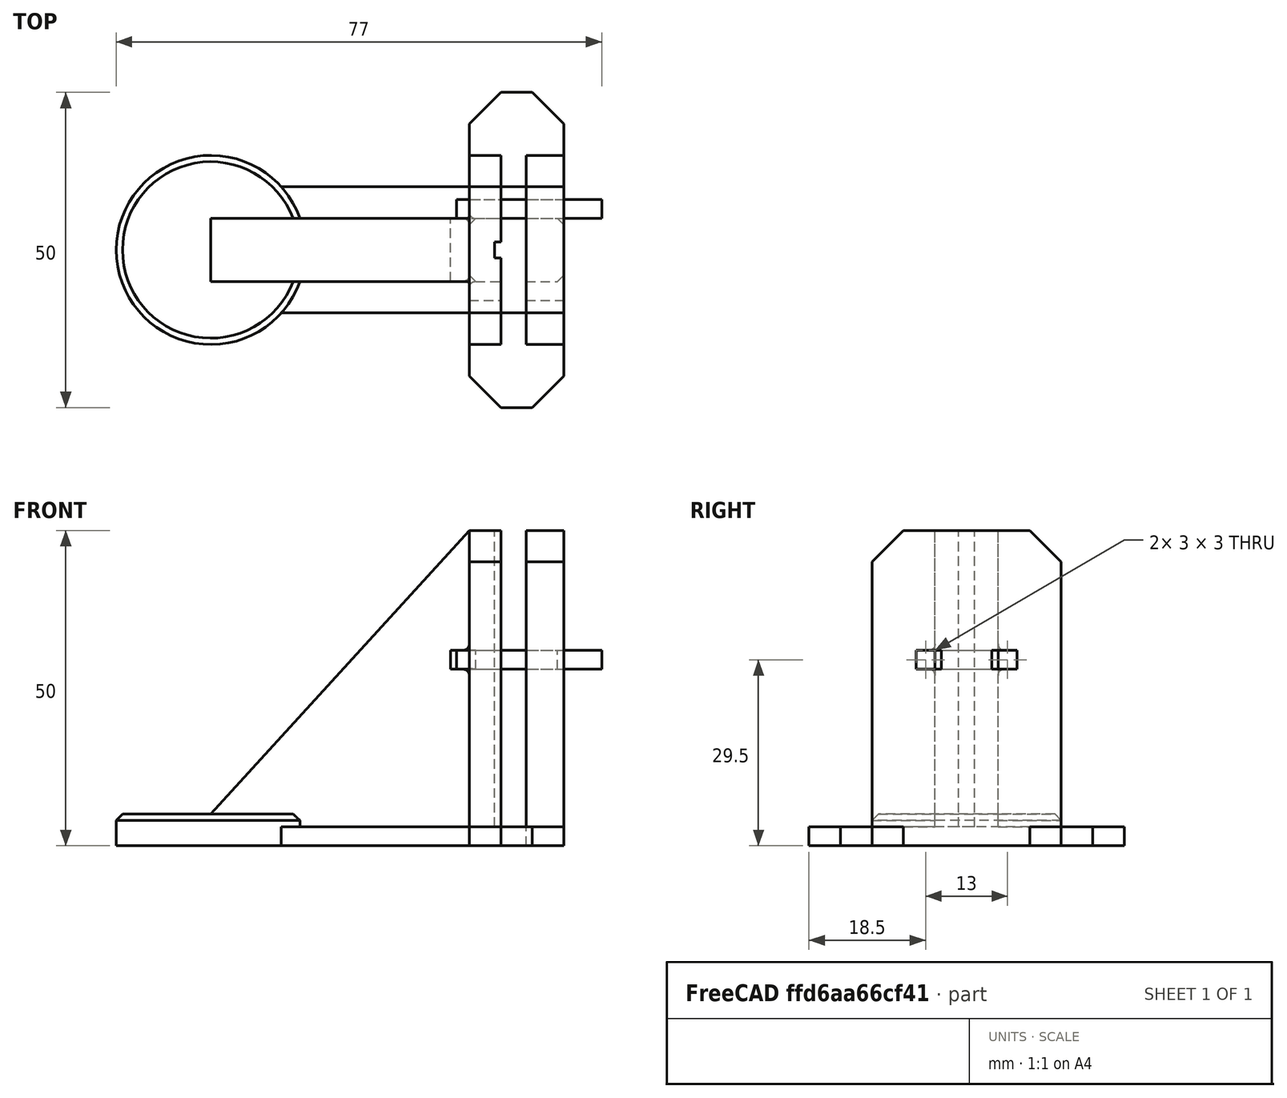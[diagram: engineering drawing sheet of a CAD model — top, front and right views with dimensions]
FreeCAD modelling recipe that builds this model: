
FCSTD DOCUMENT  (FreeCAD 0.18R16146 (Git))
Label: mesh-stand
License: All rights reserved
LicenseURL: http://en.wikipedia.org/wiki/All_rights_reserved
objects: Part::Box×11, Part::Chamfer×7, Part::Cut×3, Part::MultiFuse×2, Part::Cylinder×1
note: 24 computed .brp shape members not serialized (recipe doc carries the construction recipe); baked Part::Feature solids carry a one-line shape summary decoded from their .brp

FEATURE [Part::Box] Box  label="Cube"
  AttacherType = Attacher::AttachEngine3D
  Height = 50
  Length = 6
  Placement = pos=(0,-15,0) rot=(0,0,1;0rad)
  Width = 30
FEATURE [Part::Box] Box001  label="Cube001"
  AttacherType = Attacher::AttachEngine3D
  Height = 50
  Length = 5
  Placement = pos=(-9,-15,0) rot=(0,0,1;0rad)
  Width = 30
FEATURE [Part::Box] Box002  label="Cube002"
  AttacherType = Attacher::AttachEngine3D
  Height = 50
  Length = 5
  Placement = pos=(-5,-1.25,0) rot=(0,0,1;0rad)
  Width = 2.5
FEATURE [Part::Cut] Cut
  Base = -> Box001
  Tool = -> Box002
FEATURE [Part::Box] Box003  label="Cube003"
  AttacherType = Attacher::AttachEngine3D
  Height = 50
  Length = 44
  Placement = pos=(-50,-5,0) rot=(0,0,1;0rad)
  Width = 10
FEATURE [Part::Cylinder] Cylinder
  Angle = 360
  AttacherType = Attacher::AttachEngine3D
  Height = 5
  Placement = pos=(-50,0,0) rot=(0,0,1;0rad)
  Radius = 15
FEATURE [Part::Box] Box004  label="Cube004"
  AttacherType = Attacher::AttachEngine3D
  Height = 3
  Length = 56
  Placement = pos=(-50,-10,0) rot=(0,0,1;0rad)
  Width = 20
FEATURE [Part::Chamfer] Chamfer
  Base = -> Cylinder
  Edges = 1 edges r=1: [Edge1]
FEATURE [Part::Chamfer] Chamfer001
  Base = -> Box003
  Edges = 1 edges: [Edge2 r1=45 r2=41]
FEATURE [Part::Chamfer] Chamfer002
  Base = -> Cut
  Edges = 2 edges r=5: [Edge7,Edge8]
FEATURE [Part::Chamfer] Chamfer003
  Base = -> Box
  Edges = 2 edges r=5: [Edge10,Edge12]
FEATURE [Part::Box] Box005  label="Cube005"
  AttacherType = Attacher::AttachEngine3D
  Height = 3
  Length = 3
  Placement = pos=(-12,-10,28) rot=(0,0,1;0rad)
  Width = 20
FEATURE [Part::MultiFuse] Fusion
  Shapes = -> [Chamfer003,Chamfer,Chamfer002,Chamfer001,Box004]
FEATURE [Part::Box] Box006  label="Cube006"
  AttacherType = Attacher::AttachEngine3D
  Height = 3
  Length = 23
  Placement = pos=(-11,-8,28) rot=(0,0,1;0rad)
  Width = 3
FEATURE [Part::Cut] Cut001
  Base = -> Fusion
  Tool = -> Box005
FEATURE [Part::Box] Box007  label="Cube007"
  AttacherType = Attacher::AttachEngine3D
  Height = 3
  Length = 23
  Placement = pos=(-11,5,28) rot=(0,0,1;0rad)
  Width = 3
FEATURE [Part::Box] Box008  label="Cube008"
  AttacherType = Attacher::AttachEngine3D
  Height = 3
  Length = 23
  Placement = pos=(-11,5,28) rot=(0,0,1;0rad)
  Width = 3
FEATURE [Part::MultiFuse] Fusion001
  Shapes = -> [Box006,Box007]
FEATURE [Part::Cut] Cut002
  Base = -> Cut001
  Tool = -> Fusion001
FEATURE [Part::Chamfer] Chamfer004
  Base = -> Cut002
  Edges = 4 edges r=1: [Edge166,Edge173,Edge186,Edge198]
FEATURE [Part::Box] Box009  label="Cube009"
  AttacherType = Attacher::AttachEngine3D
  Height = 3
  Length = 15
  Placement = pos=(-9,10,0) rot=(0,0,1;0rad)
  Width = 15
FEATURE [Part::Box] Box010  label="Cube010"
  AttacherType = Attacher::AttachEngine3D
  Height = 3
  Length = 15
  Placement = pos=(-9,-25,0) rot=(0,0,1;0rad)
  Width = 15
FEATURE [Part::Chamfer] Chamfer005
  Base = -> Box010
  Edges = 2 edges r=5: [Edge1,Edge5]
FEATURE [Part::Chamfer] Chamfer006
  Base = -> Box009
  Edges = 2 edges r=5: [Edge3,Edge7]
